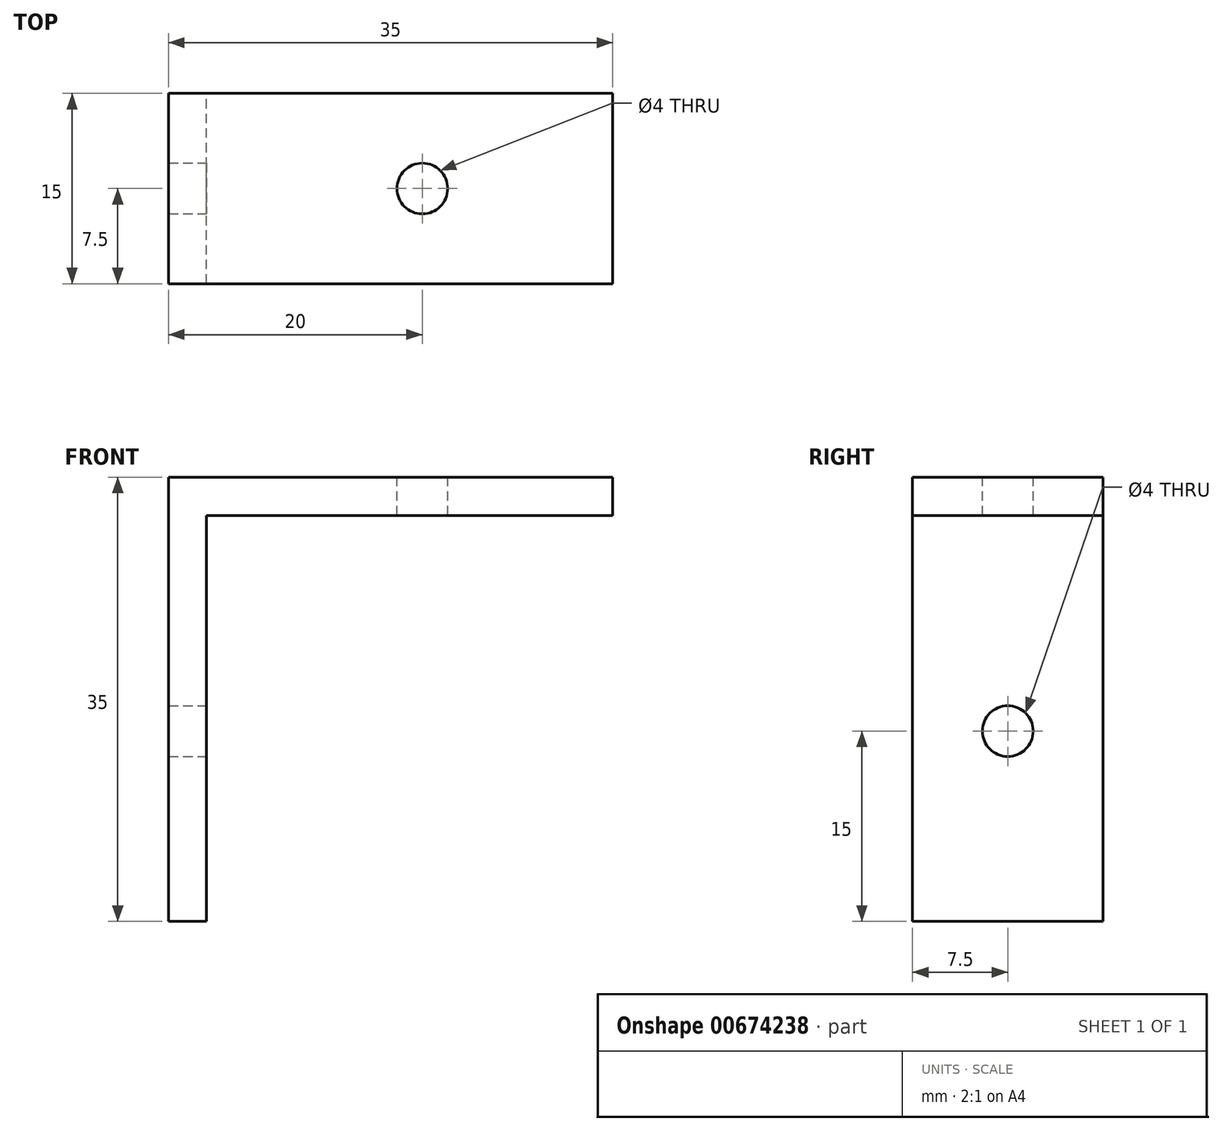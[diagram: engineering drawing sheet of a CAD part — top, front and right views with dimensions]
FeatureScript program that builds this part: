
annotation { "Feature Type Name" : "Feature", "Feature Type Description" : "" }
export const myFeature = defineFeature(function(context is Context, id is Id, definition is map)
    precondition{}
    {
        {
            var Q0;
            Q0=qCreatedBy(makeId("Front.planeOp"),FACE);
            var sketch = newSketch(context, id + "F0", { "sketchPlane" : qUnion([Q0])});
            skLineSegment(sketch, "E0.bottom", {"start": v(0, 0) * mm, "end": v(-3, 0) * mm});
            skLineSegment(sketch, "E0.top", {"start": v(0, -35) * mm, "end": v(-3, -35) * mm});
            skLineSegment(sketch, "E0.left", {"start": v(0, 0) * mm, "end": v(0, -35) * mm});
            skLineSegment(sketch, "E0.right", {"start": v(-3, 0) * mm, "end": v(-3, -35) * mm});
            skLineSegment(sketch, "E1.bottom", {"start": v(-3, 0) * mm, "end": v(32, 0) * mm});
            skLineSegment(sketch, "E1.top", {"start": v(-3, -3) * mm, "end": v(32, -3) * mm});
            skLineSegment(sketch, "E1.left", {"start": v(-3, 0) * mm, "end": v(-3, -3) * mm});
            skLineSegment(sketch, "E1.right", {"start": v(32, 0) * mm, "end": v(32, -3) * mm});
            skSolve(sketch);
        }
        {
            var Q0;
            Q0 = qSketchRegion(id + "F0", true);
            extrude(context, id + "F1", {"entities" : qUnion([Q0]), "endBound" : BoundingType.SYMMETRIC, "depth" : 15 * mm, "offsetDistance" : 25 * mm});
        }
        {
            var Q0;
            Q0=makeQuery(id+"F1.opExtrude","SWEPT_FACE",FACE,{"disambiguationData":[OSD([sQuery(id+"F0.wireOp",EDGE,"E0.left")])]});
            var sketch = newSketch(context, id + "F2", { "sketchPlane" : qUnion([Q0])});
            skLineSegment(sketch, "E2", {"start": v(0, 0) * mm, "end": v(0, -35) * mm, "construction": true});
            skCircle(sketch, "E3", {"center": v(0, -20) * mm, "radius": 2 * mm});
            skSolve(sketch);
        }
        {
            var Q0;
            Q0=makeQuery(id+"F2.imprint","IMPRINT",FACE,{"disambiguationData":[TD([[makeQuery(id+"F2.imprint","IMPRINT",EDGE,{"derivedFrom":sQuery(id+"F2.wireOp",EDGE,"E3")}),1.0]])]});
            extrude(context, id + "F3", {"entities" : qUnion([Q0]), "operationType" : NewBodyOperationType.REMOVE, "endBound" : BoundingType.THROUGH_ALL, "oppositeDirection" : true, "depth" : 25 * mm, "offsetDistance" : 25 * mm});
        }
        {
            var Q0;
            Q0=makeQuery(id+"F1.opExtrude","SWEPT_FACE",FACE,{"disambiguationData":[OSD([sQuery(id+"F0.wireOp",EDGE,"E1.bottom")])]});
            var sketch = newSketch(context, id + "F4", { "sketchPlane" : qUnion([Q0])});
            skLineSegment(sketch, "E4", {"start": v(-3, 0) * mm, "end": v(32, 0) * mm, "construction": true});
            skCircle(sketch, "E5", {"center": v(17, 0) * mm, "radius": 2 * mm});
            skSolve(sketch);
        }
        {
            var Q0;
            Q0 = qSketchRegion(id + "F4", true);
            extrude(context, id + "F5", {"entities" : qUnion([Q0]), "operationType" : NewBodyOperationType.REMOVE, "endBound" : BoundingType.THROUGH_ALL, "oppositeDirection" : true, "depth" : 25 * mm, "offsetDistance" : 25 * mm});
        }
    });
